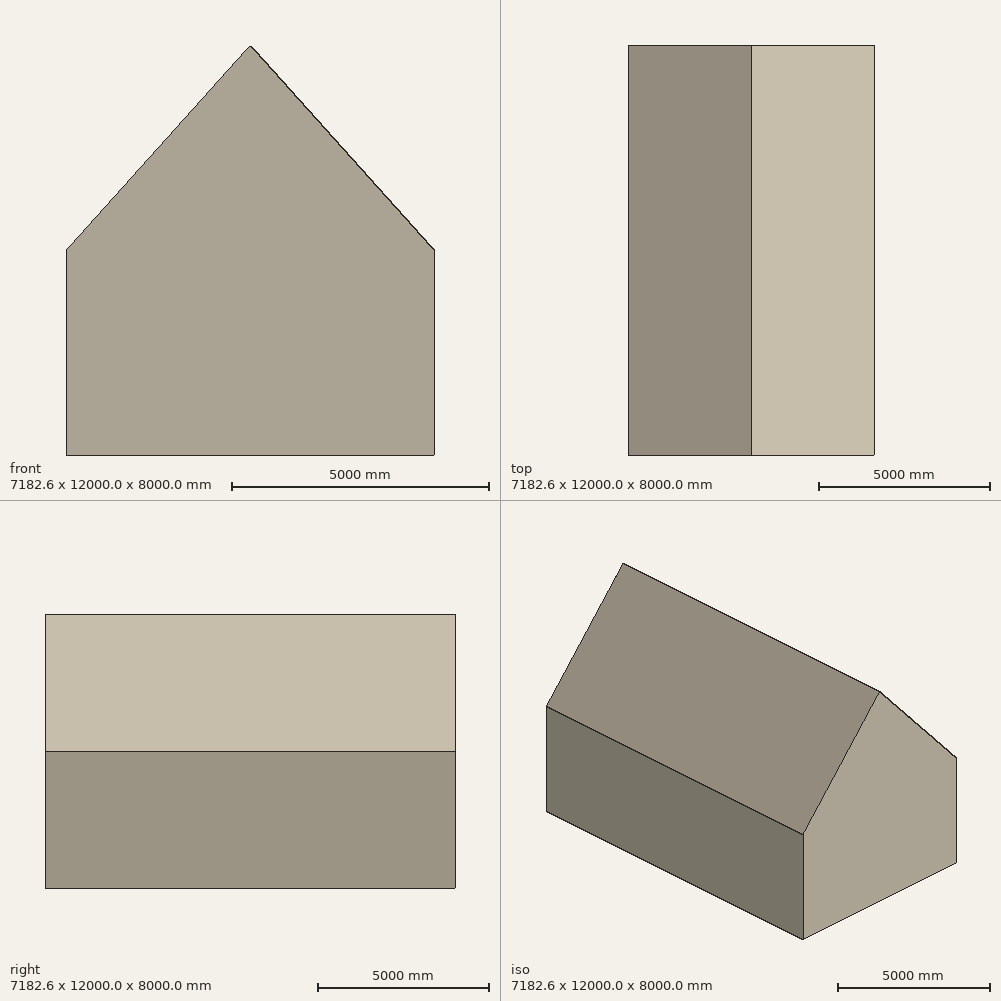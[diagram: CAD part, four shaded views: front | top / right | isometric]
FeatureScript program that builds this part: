
annotation { "Feature Type Name" : "Feature", "Feature Type Description" : "" }
export const myFeature = defineFeature(function(context is Context, id is Id, definition is map)
    precondition{}
    {
        {
            var Q0;
            Q0=qCreatedBy(makeId("Front.planeOp"),FACE);
            var sketch = newSketch(context, id + "F0", { "sketchPlane" : qUnion([Q0])});
            skLineSegment(sketch, "E0.bottom", {"start": v(-3592.23, -4179.36) * mm, "end": v(3590.37, -4179.36) * mm});
            skLineSegment(sketch, "E0.top", {"start": v(-3592.23, -179.36) * mm, "end": v(3590.37, -179.36) * mm});
            skLineSegment(sketch, "E0.left", {"start": v(-3592.23, -4179.36) * mm, "end": v(-3592.23, -179.36) * mm});
            skLineSegment(sketch, "E0.right", {"start": v(3590.37, -4179.36) * mm, "end": v(3590.37, -179.36) * mm});
            skLineSegment(sketch, "E1", {"start": v(-0.93, -179.36) * mm, "end": v(-0.93, 3820.64) * mm});
            skLineSegment(sketch, "E2", {"start": v(-3592.23, -179.36) * mm, "end": v(-0.93, 3820.64) * mm});
            skLineSegment(sketch, "E3", {"start": v(3590.37, -179.36) * mm, "end": v(-0.93, 3820.64) * mm});
            skSolve(sketch);
        }
        {
            var Q0;
            Q0 = qSketchRegion(id + "F0", true);
            extrude(context, id + "F1", {"entities" : qUnion([Q0]), "depth" : 12000 * mm});
        }
    });
